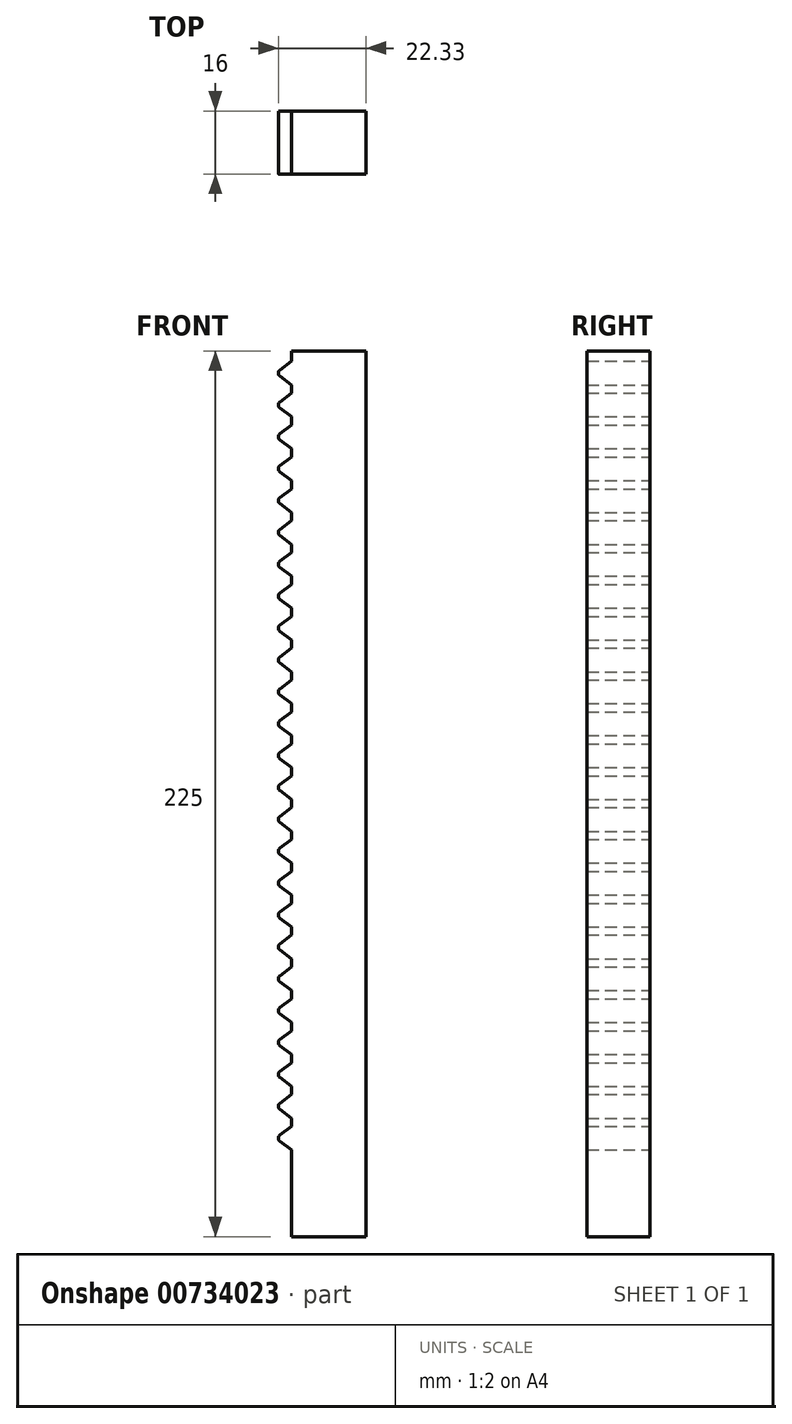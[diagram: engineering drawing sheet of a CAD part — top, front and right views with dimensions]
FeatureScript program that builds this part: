
annotation { "Feature Type Name" : "Feature", "Feature Type Description" : "" }
export const myFeature = defineFeature(function(context is Context, id is Id, definition is map)
    precondition{}
    {
        {
            var Q0;
            Q0=qCreatedBy(makeId("Top.planeOp"),FACE);
            var sketch = newSketch(context, id + "F0", { "sketchPlane" : qUnion([Q0])});
            skLineSegment(sketch, "E0.bottom", {"start": v(-5, -8) * mm, "end": v(14, -8) * mm});
            skLineSegment(sketch, "E0.top", {"start": v(-5, 8) * mm, "end": v(14, 8) * mm});
            skLineSegment(sketch, "E0.left", {"start": v(-5, -8) * mm, "end": v(-5, 8) * mm});
            skLineSegment(sketch, "E0.right", {"start": v(14, -8) * mm, "end": v(14, 8) * mm});
            skSolve(sketch);
        }
        {
            var Q0;
            Q0 = qSketchRegion(id + "F0", true);
            extrude(context, id + "F1", {"entities" : qUnion([Q0]), "depth" : 200 * mm, "offsetDistance" : 25 * mm, "hasSecondDirection" : true, "secondDirectionOppositeDirection" : true, "secondDirectionDepth" : 25 * mm});
        }
        {
            var Q0;
            Q0=qCreatedBy(makeId("Front.planeOp"),FACE);
            var sketch = newSketch(context, id + "F2", { "sketchPlane" : qUnion([Q0])});
            skLineSegment(sketch, "E1", {"start": v(-7.93, 0.8) * mm, "end": v(-5, 3) * mm});
            skLineSegment(sketch, "E2", {"start": v(-7.93, -0.8) * mm, "end": v(-5, -3) * mm});
            skPoint(sketch, "E3.visualSharp", {"position": v(-9, 0) * mm});
            skArc(sketch, "E3.filletArc", {"start": v(-7.93, 0.8) * mm, "mid": v(-8.33, 0) * mm, "end": v(-7.93, -0.8) * mm});
            skLineSegment(sketch, "E4.0.1.0", {"start": v(-7.93, 7.3) * mm, "end": v(-5, 5.1) * mm});
            skArc(sketch, "E4.0.1.1", {"start": v(-7.93, 8.9) * mm, "mid": v(-8.33, 8.1) * mm, "end": v(-7.93, 7.3) * mm});
            skLineSegment(sketch, "E4.0.1.2", {"start": v(-7.93, 8.9) * mm, "end": v(-5, 11.1) * mm});
            skLineSegment(sketch, "E4.0.2.0", {"start": v(-7.93, 15.4) * mm, "end": v(-5, 13.2) * mm});
            skArc(sketch, "E4.0.2.1", {"start": v(-7.93, 17) * mm, "mid": v(-8.33, 16.2) * mm, "end": v(-7.93, 15.4) * mm});
            skLineSegment(sketch, "E4.0.2.2", {"start": v(-7.93, 17) * mm, "end": v(-5, 19.2) * mm});
            skLineSegment(sketch, "E4.0.3.0", {"start": v(-7.93, 23.5) * mm, "end": v(-5, 21.3) * mm});
            skArc(sketch, "E4.0.3.1", {"start": v(-7.93, 25.1) * mm, "mid": v(-8.33, 24.3) * mm, "end": v(-7.93, 23.5) * mm});
            skLineSegment(sketch, "E4.0.3.2", {"start": v(-7.93, 25.1) * mm, "end": v(-5, 27.3) * mm});
            skLineSegment(sketch, "E4.0.4.0", {"start": v(-7.93, 31.6) * mm, "end": v(-5, 29.4) * mm});
            skArc(sketch, "E4.0.4.1", {"start": v(-7.93, 33.2) * mm, "mid": v(-8.33, 32.4) * mm, "end": v(-7.93, 31.6) * mm});
            skLineSegment(sketch, "E4.0.4.2", {"start": v(-7.93, 33.2) * mm, "end": v(-5, 35.4) * mm});
            skLineSegment(sketch, "E4.0.5.0", {"start": v(-7.93, 39.7) * mm, "end": v(-5, 37.5) * mm});
            skArc(sketch, "E4.0.5.1", {"start": v(-7.93, 41.3) * mm, "mid": v(-8.33, 40.5) * mm, "end": v(-7.93, 39.7) * mm});
            skLineSegment(sketch, "E4.0.5.2", {"start": v(-7.93, 41.3) * mm, "end": v(-5, 43.5) * mm});
            skLineSegment(sketch, "E4.0.6.0", {"start": v(-7.93, 47.8) * mm, "end": v(-5, 45.6) * mm});
            skArc(sketch, "E4.0.6.1", {"start": v(-7.93, 49.4) * mm, "mid": v(-8.33, 48.6) * mm, "end": v(-7.93, 47.8) * mm});
            skLineSegment(sketch, "E4.0.6.2", {"start": v(-7.93, 49.4) * mm, "end": v(-5, 51.6) * mm});
            skLineSegment(sketch, "E4.0.7.0", {"start": v(-7.93, 55.9) * mm, "end": v(-5, 53.7) * mm});
            skArc(sketch, "E4.0.7.1", {"start": v(-7.93, 57.5) * mm, "mid": v(-8.33, 56.7) * mm, "end": v(-7.93, 55.9) * mm});
            skLineSegment(sketch, "E4.0.7.2", {"start": v(-7.93, 57.5) * mm, "end": v(-5, 59.7) * mm});
            skLineSegment(sketch, "E4.0.8.0", {"start": v(-7.93, 64) * mm, "end": v(-5, 61.8) * mm});
            skArc(sketch, "E4.0.8.1", {"start": v(-7.93, 65.6) * mm, "mid": v(-8.33, 64.8) * mm, "end": v(-7.93, 64) * mm});
            skLineSegment(sketch, "E4.0.8.2", {"start": v(-7.93, 65.6) * mm, "end": v(-5, 67.8) * mm});
            skLineSegment(sketch, "E4.0.9.0", {"start": v(-7.93, 72.1) * mm, "end": v(-5, 69.9) * mm});
            skArc(sketch, "E4.0.9.1", {"start": v(-7.93, 73.7) * mm, "mid": v(-8.33, 72.9) * mm, "end": v(-7.93, 72.1) * mm});
            skLineSegment(sketch, "E4.0.9.2", {"start": v(-7.93, 73.7) * mm, "end": v(-5, 75.9) * mm});
            skLineSegment(sketch, "E4.0.10.0", {"start": v(-7.93, 80.2) * mm, "end": v(-5, 78) * mm});
            skArc(sketch, "E4.0.10.1", {"start": v(-7.93, 81.8) * mm, "mid": v(-8.33, 81) * mm, "end": v(-7.93, 80.2) * mm});
            skLineSegment(sketch, "E4.0.10.2", {"start": v(-7.93, 81.8) * mm, "end": v(-5, 84) * mm});
            skLineSegment(sketch, "E4.0.11.0", {"start": v(-7.93, 88.3) * mm, "end": v(-5, 86.1) * mm});
            skArc(sketch, "E4.0.11.1", {"start": v(-7.93, 89.9) * mm, "mid": v(-8.33, 89.1) * mm, "end": v(-7.93, 88.3) * mm});
            skLineSegment(sketch, "E4.0.11.2", {"start": v(-7.93, 89.9) * mm, "end": v(-5, 92.1) * mm});
            skLineSegment(sketch, "E4.0.12.0", {"start": v(-7.93, 96.4) * mm, "end": v(-5, 94.2) * mm});
            skArc(sketch, "E4.0.12.1", {"start": v(-7.93, 98) * mm, "mid": v(-8.33, 97.2) * mm, "end": v(-7.93, 96.4) * mm});
            skLineSegment(sketch, "E4.0.12.2", {"start": v(-7.93, 98) * mm, "end": v(-5, 100.2) * mm});
            skLineSegment(sketch, "E4.0.13.0", {"start": v(-7.93, 104.5) * mm, "end": v(-5, 102.3) * mm});
            skArc(sketch, "E4.0.13.1", {"start": v(-7.93, 106.1) * mm, "mid": v(-8.33, 105.3) * mm, "end": v(-7.93, 104.5) * mm});
            skLineSegment(sketch, "E4.0.13.2", {"start": v(-7.93, 106.1) * mm, "end": v(-5, 108.3) * mm});
            skLineSegment(sketch, "E4.0.14.0", {"start": v(-7.93, 112.6) * mm, "end": v(-5, 110.4) * mm});
            skArc(sketch, "E4.0.14.1", {"start": v(-7.93, 114.2) * mm, "mid": v(-8.33, 113.4) * mm, "end": v(-7.93, 112.6) * mm});
            skLineSegment(sketch, "E4.0.14.2", {"start": v(-7.93, 114.2) * mm, "end": v(-5, 116.4) * mm});
            skLineSegment(sketch, "E4.0.15.0", {"start": v(-7.93, 120.7) * mm, "end": v(-5, 118.5) * mm});
            skArc(sketch, "E4.0.15.1", {"start": v(-7.93, 122.3) * mm, "mid": v(-8.33, 121.5) * mm, "end": v(-7.93, 120.7) * mm});
            skLineSegment(sketch, "E4.0.15.2", {"start": v(-7.93, 122.3) * mm, "end": v(-5, 124.5) * mm});
            skLineSegment(sketch, "E4.0.16.0", {"start": v(-7.93, 128.8) * mm, "end": v(-5, 126.6) * mm});
            skArc(sketch, "E4.0.16.1", {"start": v(-7.93, 130.4) * mm, "mid": v(-8.33, 129.6) * mm, "end": v(-7.93, 128.8) * mm});
            skLineSegment(sketch, "E4.0.16.2", {"start": v(-7.93, 130.4) * mm, "end": v(-5, 132.6) * mm});
            skLineSegment(sketch, "E4.0.17.0", {"start": v(-7.93, 136.9) * mm, "end": v(-5, 134.7) * mm});
            skArc(sketch, "E4.0.17.1", {"start": v(-7.93, 138.5) * mm, "mid": v(-8.33, 137.7) * mm, "end": v(-7.93, 136.9) * mm});
            skLineSegment(sketch, "E4.0.17.2", {"start": v(-7.93, 138.5) * mm, "end": v(-5, 140.7) * mm});
            skLineSegment(sketch, "E4.0.18.0", {"start": v(-7.93, 145) * mm, "end": v(-5, 142.8) * mm});
            skArc(sketch, "E4.0.18.1", {"start": v(-7.93, 146.6) * mm, "mid": v(-8.33, 145.8) * mm, "end": v(-7.93, 145) * mm});
            skLineSegment(sketch, "E4.0.18.2", {"start": v(-7.93, 146.6) * mm, "end": v(-5, 148.8) * mm});
            skLineSegment(sketch, "E4.0.19.0", {"start": v(-7.93, 153.1) * mm, "end": v(-5, 150.9) * mm});
            skArc(sketch, "E4.0.19.1", {"start": v(-7.93, 154.7) * mm, "mid": v(-8.33, 153.9) * mm, "end": v(-7.93, 153.1) * mm});
            skLineSegment(sketch, "E4.0.19.2", {"start": v(-7.93, 154.7) * mm, "end": v(-5, 156.9) * mm});
            skLineSegment(sketch, "E4.direction1", {"start": v(-7.93, -0.8) * mm, "end": v(16.07, -0.8) * mm, "construction": true});
            skLineSegment(sketch, "E4.direction2", {"start": v(-7.93, -0.8) * mm, "end": v(-7.93, 7.3) * mm, "construction": true});
            skLineSegment(sketch, "E5.0.0.20", {"start": v(-7.93, 161.2) * mm, "end": v(-5, 159) * mm});
            skArc(sketch, "E5.3.0.20", {"start": v(-7.93, 162.8) * mm, "mid": v(-8.33, 162) * mm, "end": v(-7.93, 161.2) * mm});
            skLineSegment(sketch, "E5.7.0.20", {"start": v(-7.93, 162.8) * mm, "end": v(-5, 165) * mm});
            skLineSegment(sketch, "E5.0.0.21", {"start": v(-7.93, 169.3) * mm, "end": v(-5, 167.1) * mm});
            skArc(sketch, "E5.3.0.21", {"start": v(-7.93, 170.9) * mm, "mid": v(-8.33, 170.1) * mm, "end": v(-7.93, 169.3) * mm});
            skLineSegment(sketch, "E5.7.0.21", {"start": v(-7.93, 170.9) * mm, "end": v(-5, 173.1) * mm});
            skLineSegment(sketch, "E6.0.0.22", {"start": v(-7.93, 177.4) * mm, "end": v(-5, 175.2) * mm});
            skArc(sketch, "E6.3.0.22", {"start": v(-7.93, 179) * mm, "mid": v(-8.33, 178.2) * mm, "end": v(-7.93, 177.4) * mm});
            skLineSegment(sketch, "E6.7.0.22", {"start": v(-7.93, 179) * mm, "end": v(-5, 181.2) * mm});
            skLineSegment(sketch, "E6.0.0.23", {"start": v(-7.93, 185.5) * mm, "end": v(-5, 183.3) * mm});
            skArc(sketch, "E6.3.0.23", {"start": v(-7.93, 187.1) * mm, "mid": v(-8.33, 186.3) * mm, "end": v(-7.93, 185.5) * mm});
            skLineSegment(sketch, "E6.7.0.23", {"start": v(-7.93, 187.1) * mm, "end": v(-5, 189.3) * mm});
            skLineSegment(sketch, "E7.0.0.24", {"start": v(-7.93, 193.6) * mm, "end": v(-5, 191.4) * mm});
            skArc(sketch, "E7.3.0.24", {"start": v(-7.93, 195.2) * mm, "mid": v(-8.33, 194.4) * mm, "end": v(-7.93, 193.6) * mm});
            skLineSegment(sketch, "E7.7.0.24", {"start": v(-7.93, 195.2) * mm, "end": v(-5, 197.4) * mm});
            skLineSegment(sketch, "E8", {"start": v(-5, -3) * mm, "end": v(-5, 197.4) * mm});
            skSolve(sketch);
        }
        {
            var Q0;
            Q0 = qSketchRegion(id + "F2", true);
            extrude(context, id + "F3", {"entities" : qUnion([Q0]), "operationType" : NewBodyOperationType.ADD, "endBound" : BoundingType.SYMMETRIC, "depth" : 16 * mm, "offsetDistance" : 25 * mm});
        }
    });
